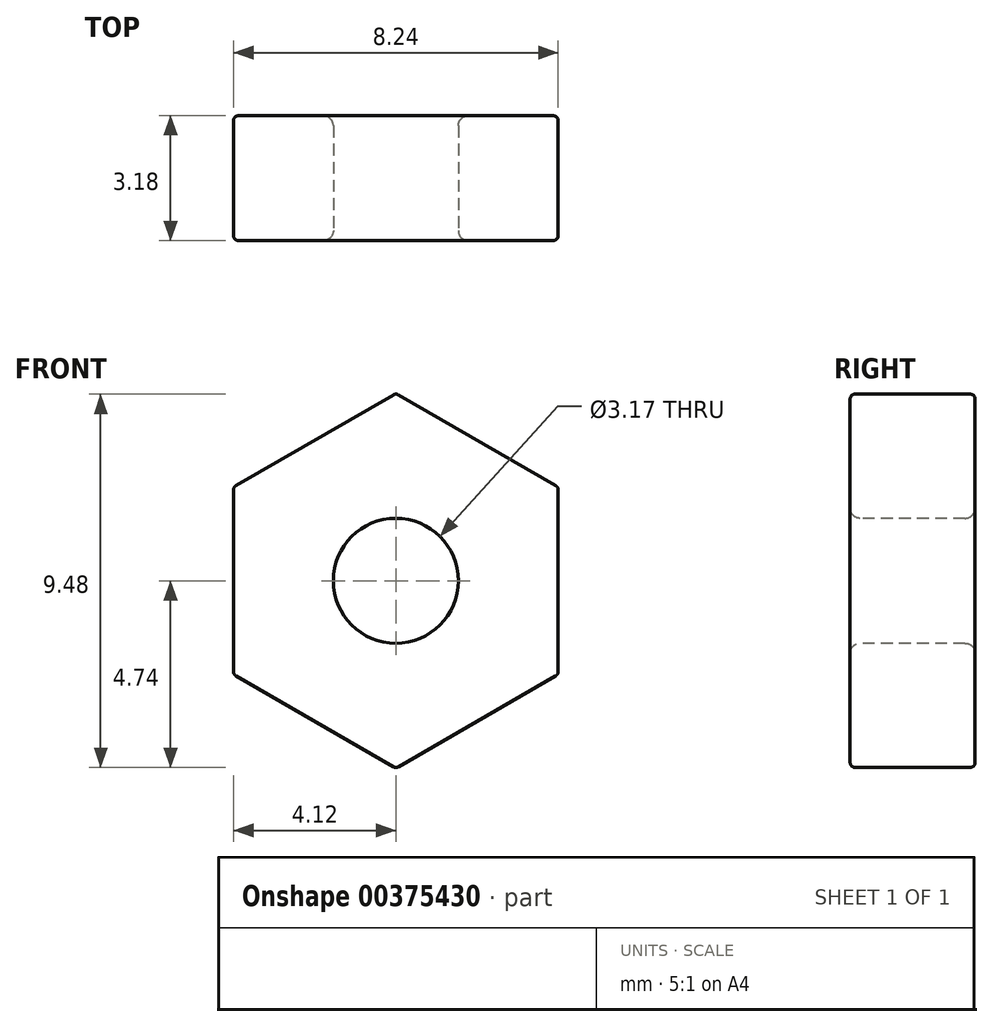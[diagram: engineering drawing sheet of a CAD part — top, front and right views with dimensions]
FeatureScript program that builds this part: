
annotation { "Feature Type Name" : "Feature", "Feature Type Description" : "" }
export const myFeature = defineFeature(function(context is Context, id is Id, definition is map)
    precondition{}
    {
        {
            var Q0;
            Q0=qCreatedBy(makeId("Front.planeOp"),FACE);
            var sketch = newSketch(context, id + "F0", { "sketchPlane" : qUnion([Q0])});
            skCircle(sketch, "E0.cCircle", {"center": v(0, 0) * mm, "radius": 4.12 * mm, "construction": true});
            skLineSegment(sketch, "E0.0", {"start": v(0, 4.76) * mm, "end": v(4.12, 2.38) * mm});
            skLineSegment(sketch, "E0.1", {"start": v(4.12, 2.38) * mm, "end": v(4.12, -2.38) * mm});
            skLineSegment(sketch, "E0.2", {"start": v(4.12, -2.38) * mm, "end": v(0, -4.76) * mm});
            skLineSegment(sketch, "E0.3", {"start": v(0, -4.76) * mm, "end": v(-4.12, -2.38) * mm});
            skLineSegment(sketch, "E0.4", {"start": v(-4.12, -2.38) * mm, "end": v(-4.12, 2.38) * mm});
            skLineSegment(sketch, "E0.5", {"start": v(-4.12, 2.38) * mm, "end": v(0, 4.76) * mm});
            skPoint(sketch, "E0.0.midPoint", {"position": v(2.06, 3.57) * mm});
            skSolve(sketch);
        }
        {
            var Q0;
            Q0=qSketchRegion(id+"F0",true);
            extrude(context, id + "F1", {"entities" : qUnion([Q0]), "depth" : 3.17 * mm, "symmetric" : true});
        }
        {
            var Q0;
            Q0=makeQuery(id+"F1.opExtrude","CAP_FACE",FACE,{"disambiguationData":[OSD([sQuery(id+"F0.wireOp",EDGE,"E0.0"),sQuery(id+"F0.wireOp",EDGE,"E0.1"),sQuery(id+"F0.wireOp",EDGE,"E0.2"),sQuery(id+"F0.wireOp",EDGE,"E0.3"),sQuery(id+"F0.wireOp",EDGE,"E0.4"),sQuery(id+"F0.wireOp",EDGE,"E0.5")])],"isStart":false});
            var sketch = newSketch(context, id + "F2", { "sketchPlane" : qUnion([Q0])});
            skCircle(sketch, "E1", {"center": v(0, 0) * mm, "radius": 1.59 * mm});
            skSolve(sketch);
        }
        {
            var Q0;
            Q0=qSketchRegion(id+"F2",true);
            extrude(context, id + "F3", {"entities" : qUnion([Q0]), "operationType" : NewBodyOperationType.REMOVE, "endBound" : BoundingType.THROUGH_ALL, "oppositeDirection" : true, "depth" : 25.4 * mm});
        }
        {
            var Q0;
            Q0=makeQuery(id+"F1.opExtrude","CAP_EDGE",EDGE,{"disambiguationData":[OSD([sQuery(id+"F0.wireOp",EDGE,"E0.5")])],"isStart":false});
            var Q1;
            Q1=makeQuery(id+"F1.opExtrude","CAP_EDGE",EDGE,{"disambiguationData":[OSD([sQuery(id+"F0.wireOp",EDGE,"E0.4")])],"isStart":false});
            var Q2;
            Q2=makeQuery(id+"F1.opExtrude","CAP_EDGE",EDGE,{"disambiguationData":[OSD([sQuery(id+"F0.wireOp",EDGE,"E0.0")])],"isStart":false});
            var Q3;
            Q3=makeQuery(id+"F1.opExtrude","CAP_EDGE",EDGE,{"disambiguationData":[OSD([sQuery(id+"F0.wireOp",EDGE,"E0.3")])],"isStart":false});
            var Q4;
            Q4=makeQuery(id+"F1.opExtrude","CAP_EDGE",EDGE,{"disambiguationData":[OSD([sQuery(id+"F0.wireOp",EDGE,"E0.2")])],"isStart":false});
            var Q5;
            Q5=makeQuery(id+"F1.opExtrude","CAP_EDGE",EDGE,{"disambiguationData":[OSD([sQuery(id+"F0.wireOp",EDGE,"E0.1")])],"isStart":false});
            var Q6;
            Q6=makeQuery(id+"F1.opExtrude","SWEPT_EDGE",EDGE,{"disambiguationData":[OSD([sQuery(id+"F0.wireOp",EDGE,"E0.0"),sQuery(id+"F0.wireOp",EDGE,"E0.1")])]});
            var Q7;
            Q7=makeQuery(id+"F1.opExtrude","SWEPT_EDGE",EDGE,{"disambiguationData":[OSD([sQuery(id+"F0.wireOp",EDGE,"E0.0"),sQuery(id+"F0.wireOp",EDGE,"E0.5")])]});
            var Q8;
            Q8=makeQuery(id+"F1.opExtrude","CAP_EDGE",EDGE,{"disambiguationData":[OSD([sQuery(id+"F0.wireOp",EDGE,"E0.1")])],"isStart":true});
            var Q9;
            Q9=makeQuery(id+"F1.opExtrude","CAP_EDGE",EDGE,{"disambiguationData":[OSD([sQuery(id+"F0.wireOp",EDGE,"E0.0")])],"isStart":true});
            var Q10;
            Q10=makeQuery(id+"F1.opExtrude","CAP_EDGE",EDGE,{"disambiguationData":[OSD([sQuery(id+"F0.wireOp",EDGE,"E0.4")])],"isStart":true});
            var Q11;
            Q11=makeQuery(id+"F1.opExtrude","CAP_EDGE",EDGE,{"disambiguationData":[OSD([sQuery(id+"F0.wireOp",EDGE,"E0.5")])],"isStart":true});
            var Q12;
            Q12=makeQuery(id+"F1.opExtrude","CAP_EDGE",EDGE,{"disambiguationData":[OSD([sQuery(id+"F0.wireOp",EDGE,"E0.2")])],"isStart":true});
            var Q13;
            Q13=makeQuery(id+"F1.opExtrude","SWEPT_EDGE",EDGE,{"disambiguationData":[OSD([sQuery(id+"F0.wireOp",EDGE,"E0.1"),sQuery(id+"F0.wireOp",EDGE,"E0.2")])]});
            var Q14;
            Q14=makeQuery(id+"F1.opExtrude","CAP_EDGE",EDGE,{"disambiguationData":[OSD([sQuery(id+"F0.wireOp",EDGE,"E0.3")])],"isStart":true});
            var Q15;
            Q15=makeQuery(id+"F1.opExtrude","SWEPT_EDGE",EDGE,{"disambiguationData":[OSD([sQuery(id+"F0.wireOp",EDGE,"E0.2"),sQuery(id+"F0.wireOp",EDGE,"E0.3")])]});
            var Q16;
            Q16=makeQuery(id+"F1.opExtrude","SWEPT_EDGE",EDGE,{"disambiguationData":[OSD([sQuery(id+"F0.wireOp",EDGE,"E0.3"),sQuery(id+"F0.wireOp",EDGE,"E0.4")])]});
            var Q17;
            Q17=makeQuery(id+"F1.opExtrude","SWEPT_EDGE",EDGE,{"disambiguationData":[OSD([sQuery(id+"F0.wireOp",EDGE,"E0.4"),sQuery(id+"F0.wireOp",EDGE,"E0.5")])]});
            fillet(context, id + "F4", {"entities" : qUnion([Q0, Q1, Q2, Q3, Q4, Q5, Q6, Q7, Q8, Q9, Q10, Q11, Q12, Q13, Q14, Q15, Q16, Q17]), "radius" : 0.13 * mm, "tangentPropagation" : true, "allowEdgeOverflow" : false});
        }
        {
            var Q0;
            Q0=makeQuery(id+"F1.opExtrude","CAP_FACE",FACE,{"disambiguationData":[OSD([sQuery(id+"F0.wireOp",EDGE,"E0.0"),sQuery(id+"F0.wireOp",EDGE,"E0.1"),sQuery(id+"F0.wireOp",EDGE,"E0.2"),sQuery(id+"F0.wireOp",EDGE,"E0.3"),sQuery(id+"F0.wireOp",EDGE,"E0.4"),sQuery(id+"F0.wireOp",EDGE,"E0.5")])],"isStart":false});
            var Q1;
            Q1=makeQuery(id+"F3.boolean.opBoolean","COPY",FACE,{"derivedFrom":makeQuery(id+"F3.opExtrude","SWEPT_FACE",FACE,{"disambiguationData":[OSD([sQuery(id+"F2.wireOp",EDGE,"E1")])]})});
            fillet(context, id + "F5", {"entities" : qUnion([Q0, Q1]), "radius" : 0.25 * mm, "tangentPropagation" : true, "allowEdgeOverflow" : false});
        }
    });
